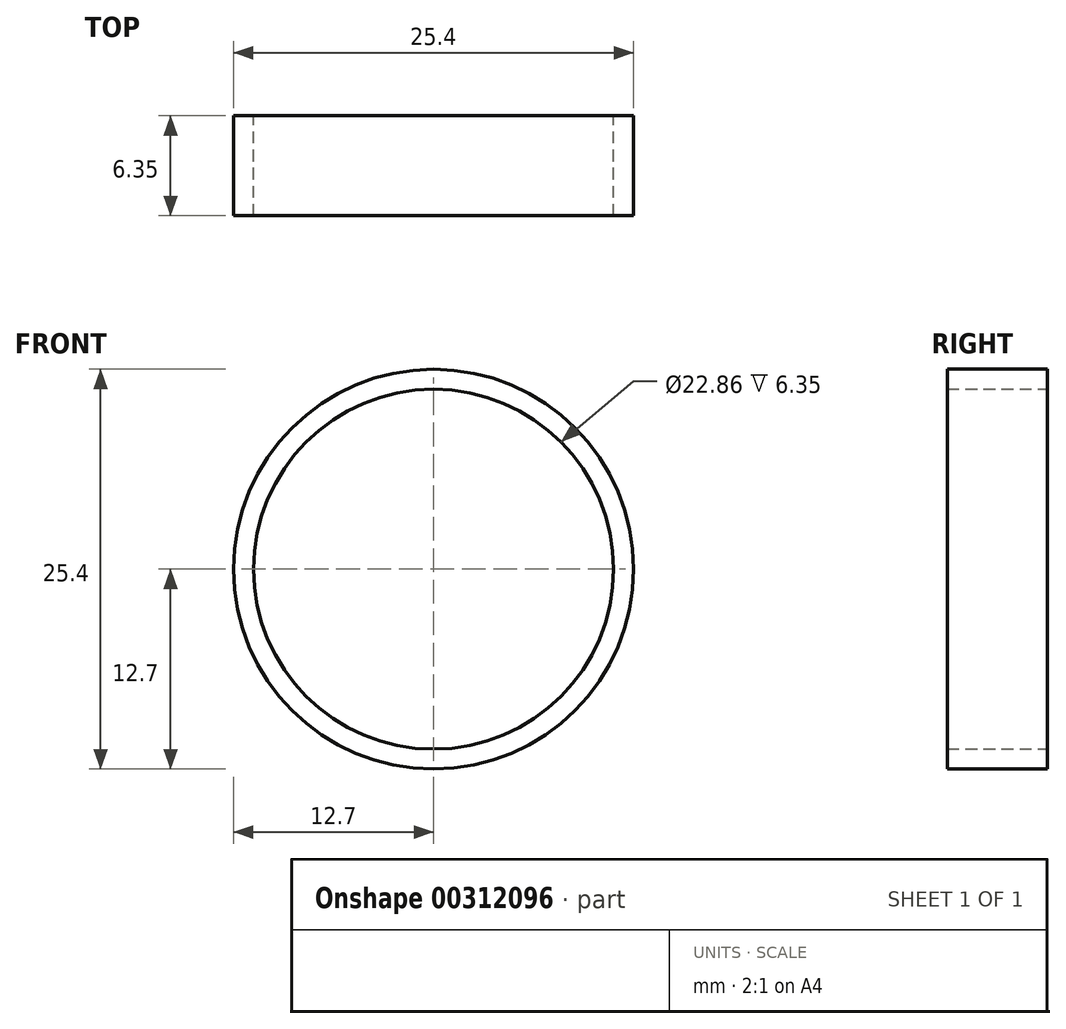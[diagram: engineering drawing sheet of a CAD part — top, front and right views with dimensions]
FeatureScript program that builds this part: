
annotation { "Feature Type Name" : "Feature", "Feature Type Description" : "" }
export const myFeature = defineFeature(function(context is Context, id is Id, definition is map)
    precondition{}
    {
        {
            var Q0;
            Q0=qCreatedBy(makeId("Front.planeOp"),FACE);
            var sketch = newSketch(context, id + "F0", { "sketchPlane" : qUnion([Q0])});
            skCircle(sketch, "E0", {"center": v(0, 0) * mm, "radius": 12.7 * mm});
            skCircle(sketch, "E1", {"center": v(0, 0) * mm, "radius": 11.43 * mm});
            skSolve(sketch);
        }
        {
            var Q0;
            Q0 = qSketchRegion(id + "F0", true);
            extrude(context, id + "F1", {"entities" : qUnion([Q0]), "depth" : 6.35 * mm});
        }
    });
